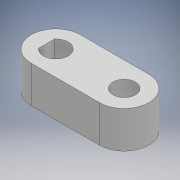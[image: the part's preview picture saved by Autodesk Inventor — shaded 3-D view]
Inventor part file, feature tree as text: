
AUTODESK INVENTOR PART (.ipt)
format: ipt  version: 2017 (Build 210142000, 142)  size: 111,104 bytes
history: native  units: mm
features: extrude x2, sketch x2
ambient origin geometry x8: Origin, YZ Plane, XZ Plane, XY Plane, X Axis, Y Axis, Z Axis, Center Point
bodies: Solid1 (feature_tree)
feature tree (4):
  extrude  "Extrusion1"  Depth=8.0mm
  extrude  "Extrusion2"  Depth=16.0mm
  sketch  "Sketch1"  dims[d0=22.225mm d1=8.0mm]
  sketch  "Sketch2"  dims[d2=7.3mm d3=16.0mm d4=12.0mm d5=0.0mm d6=7.0mm d7=12.0mm d8=0.0mm]
